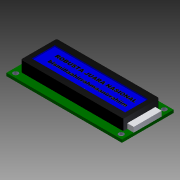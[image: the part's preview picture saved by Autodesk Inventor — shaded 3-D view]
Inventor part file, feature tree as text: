
AUTODESK INVENTOR PART (.ipt)
format: ipt  version: 2015 (Build 190159000, 159)  size: 179,200 bytes
history: native  units: in
note: dims shown in document units (in); Inventor stores cm internally (conversion verified against a paired STEP export)
features: other x2, sketch x1, imported_body x1
ambient origin geometry x8: Origin, YZ Plane, XZ Plane, XY Plane, X Axis, Y Axis, Z Axis, Center Point
bodies: Body1 (feature_tree)
feature tree (4):
  other  "Boss-Extrude5"
  other  "LCD 16x21"
  sketch  "Sketch1"
  imported_body  "Base1"
